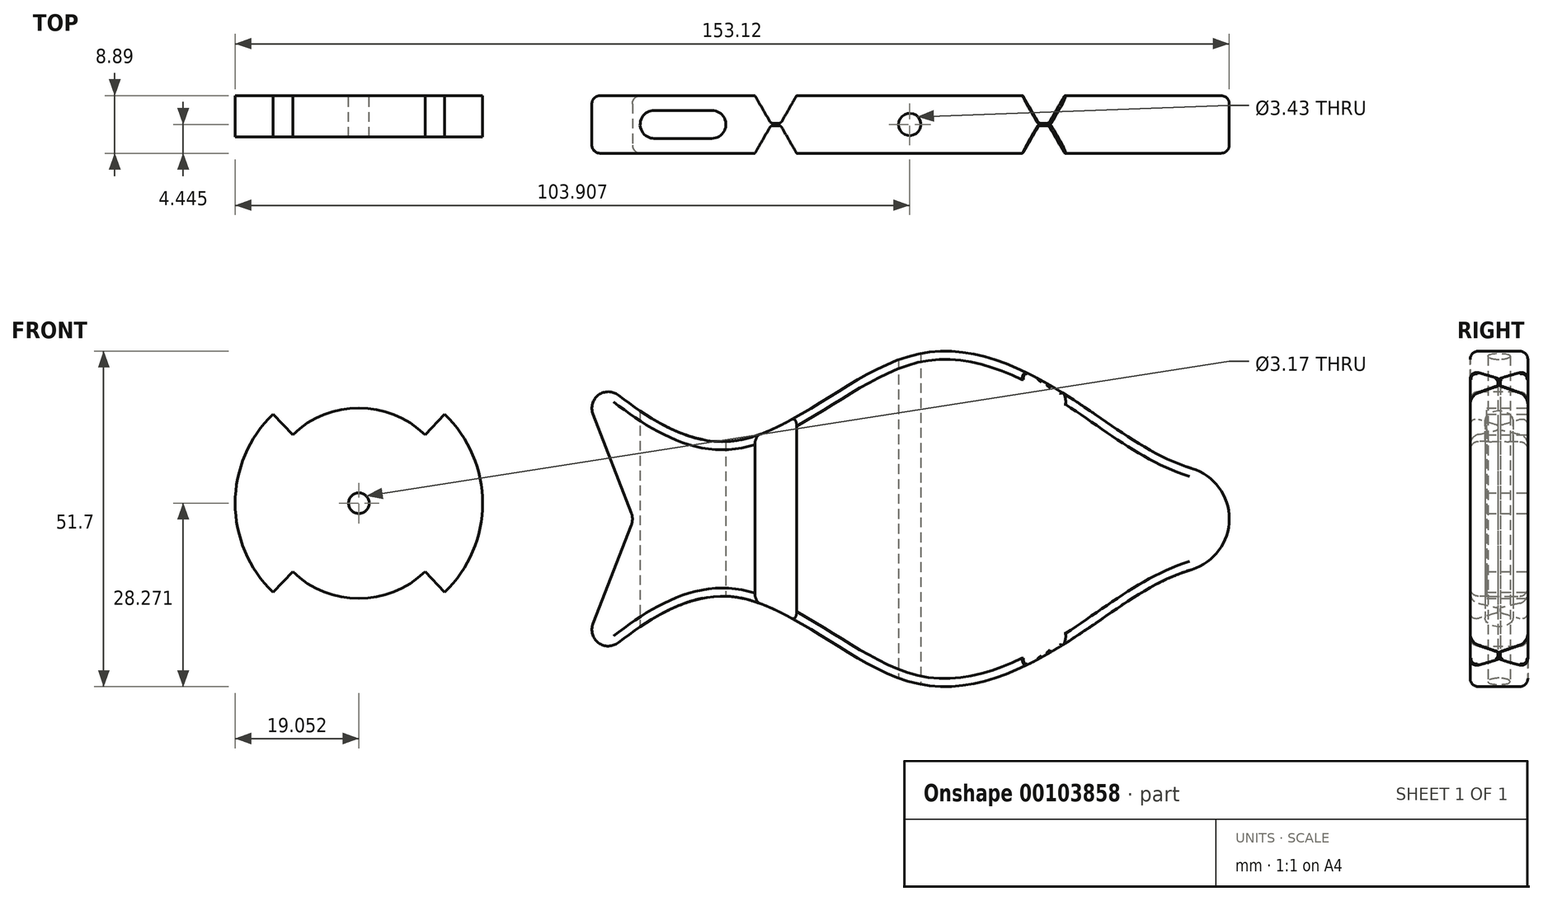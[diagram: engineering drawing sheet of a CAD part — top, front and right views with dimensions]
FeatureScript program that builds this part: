
annotation { "Feature Type Name" : "Feature", "Feature Type Description" : "" }
export const myFeature = defineFeature(function(context is Context, id is Id, definition is map)
    precondition{}
    {
        {
            var Q0;
            Q0=qCreatedBy(makeId("Front.planeOp"),FACE);
            var sketch = newSketch(context, id + "F0", { "sketchPlane" : qUnion([Q0])});
            skLineSegment(sketch, "E0.bottom", {"start": v(0, 0) * mm, "end": v(101.6, 0) * mm, "construction": true});
            skLineSegment(sketch, "E0.top", {"start": v(0, 50.8) * mm, "end": v(101.6, 50.8) * mm, "construction": true});
            skLineSegment(sketch, "E0.left", {"start": v(0, 0) * mm, "end": v(0, 50.8) * mm, "construction": true});
            skLineSegment(sketch, "E0.right", {"start": v(101.6, 0) * mm, "end": v(101.6, 50.8) * mm, "construction": true});
            skArc(sketch, "E1", {"start": v(101.6, 25.4) * mm, "mid": v(100, 30.23) * mm, "end": v(95.86, 33.18) * mm});
            skPoint(sketch, "E1.centerSnap0", {"position": v(101.6, 25.4) * mm});
            skFitSpline(sketch, "E2", {"points": [v(95.86, 33.18) * mm, v(77.9, 43.57) * mm, v(53.58, 50.8) * mm, v(25.25, 37.41) * mm, v(0, 50.8) * mm], "startDerivative": vector(-90.13, 27.78) * mm, "endDerivative": vector(-94.96, 83.29) * mm});
            skLineSegment(sketch, "E3", {"start": v(101.6, 25.4) * mm, "end": v(0, 25.4) * mm, "construction": true});
            skFitSpline(sketch, "E4.MirrorCS", {"points": [v(95.86, 17.62) * mm, v(77.9, 7.23) * mm, v(53.58, 0) * mm, v(25.25, 13.39) * mm, v(0, 0) * mm], "startDerivative": vector(-90.13, -27.78) * mm, "endDerivative": vector(-94.96, -83.29) * mm});
            skArc(sketch, "E5.MirrorCS", {"start": v(101.6, 25.4) * mm, "mid": v(100, 20.57) * mm, "end": v(95.86, 17.62) * mm});
            skLineSegment(sketch, "E6", {"start": v(0, 50.8) * mm, "end": v(9.85, 25.4) * mm});
            skLineSegment(sketch, "E7", {"start": v(9.85, 25.4) * mm, "end": v(0, 0) * mm});
            skSolve(sketch);
        }
        {
            var Q0;
            Q0=makeQuery(id+"F0.imprint","IMPRINT",FACE,{"disambiguationData":[TD([[makeQuery(id+"F0.imprint","IMPRINT",EDGE,{"derivedFrom":sQuery(id+"F0.wireOp",EDGE,"E1")}),1.0]])]});
            extrude(context, id + "F1", {"entities" : qUnion([Q0]), "depth" : 8.9 * mm});
        }
        {
            var Q0;
            Q0=qCreatedBy(makeId("Top.planeOp"),FACE);
            var sketch = newSketch(context, id + "F2", { "sketchPlane" : qUnion([Q0])});
            skFitSpline(sketch, "E8.0", {"points": [v(95.86, -8.9) * mm, v(89.2, -8.9) * mm, v(78.75, -8.9) * mm, v(52.6, -8.9) * mm, v(25.22, -8.9) * mm, v(8.24, -8.9) * mm, v(0, -8.9) * mm], "construction": true});
            skFitSpline(sketch, "E9.0", {"points": [v(95.86, 0) * mm, v(89.2, 0) * mm, v(78.75, 0) * mm, v(52.6, 0) * mm, v(25.22, 0) * mm, v(8.24, 0) * mm, v(0, 0) * mm], "construction": true});
            skLineSegment(sketch, "E10", {"start": v(0, 0) * mm, "end": v(0, -8.9) * mm, "construction": true});
            skLineSegment(sketch, "E11", {"start": v(0, -4.45) * mm, "end": v(95.86, -4.45) * mm, "construction": true});
            skLineSegment(sketch, "E12", {"start": v(28.53, 0) * mm, "end": v(30.99, -4.25) * mm});
            skLineSegment(sketch, "E13", {"start": v(30.99, -4.25) * mm, "end": v(32.51, -4.25) * mm});
            skLineSegment(sketch, "E14", {"start": v(32.51, -4.25) * mm, "end": v(34.97, 0) * mm});
            skLineSegment(sketch, "E15", {"start": v(31.75, -4.25) * mm, "end": v(31.75, 0) * mm, "construction": true});
            skLineSegment(sketch, "E16", {"start": v(28.53, 0) * mm, "end": v(34.97, 0) * mm});
            skLineSegment(sketch, "E17.MirrorCS", {"start": v(30.99, -4.64) * mm, "end": v(32.51, -4.64) * mm});
            skLineSegment(sketch, "E18.MirrorCS", {"start": v(32.51, -4.64) * mm, "end": v(34.97, -8.9) * mm});
            skLineSegment(sketch, "E19.MirrorCS", {"start": v(28.53, -8.9) * mm, "end": v(34.97, -8.9) * mm});
            skLineSegment(sketch, "E20.MirrorCS", {"start": v(28.53, -8.9) * mm, "end": v(30.99, -4.64) * mm});
            skLineSegment(sketch, "E21.MirrorCS", {"start": v(31.75, -4.64) * mm, "end": v(31.75, -8.9) * mm, "construction": true});
            skLineSegment(sketch, "E22.1.0.0", {"start": v(73.03, -4.64) * mm, "end": v(73.03, -8.9) * mm, "construction": true});
            skLineSegment(sketch, "E22.1.0.1", {"start": v(69.8, 0) * mm, "end": v(76.24, 0) * mm});
            skLineSegment(sketch, "E22.1.0.2", {"start": v(73.79, -4.64) * mm, "end": v(76.24, -8.9) * mm});
            skLineSegment(sketch, "E22.1.0.3", {"start": v(69.8, -8.9) * mm, "end": v(76.24, -8.9) * mm});
            skLineSegment(sketch, "E22.1.0.4", {"start": v(73.79, -4.25) * mm, "end": v(76.24, 0) * mm});
            skLineSegment(sketch, "E22.1.0.5", {"start": v(69.8, 0) * mm, "end": v(72.26, -4.25) * mm});
            skLineSegment(sketch, "E22.1.0.6", {"start": v(73.03, -4.25) * mm, "end": v(73.03, 0) * mm, "construction": true});
            skLineSegment(sketch, "E22.1.0.7", {"start": v(69.8, -8.89) * mm, "end": v(72.26, -4.64) * mm});
            skLineSegment(sketch, "E22.1.0.8", {"start": v(72.26, -4.64) * mm, "end": v(73.79, -4.64) * mm});
            skLineSegment(sketch, "E22.1.0.9", {"start": v(72.26, -4.25) * mm, "end": v(73.79, -4.25) * mm});
            skLineSegment(sketch, "E22.direction1", {"start": v(28.53, -8.9) * mm, "end": v(69.8, -8.9) * mm, "construction": true});
            skLineSegment(sketch, "E23", {"start": v(31.75, 0) * mm, "end": v(73.03, 0) * mm, "construction": true});
            skLineSegment(sketch, "E24", {"start": v(52.39, 0) * mm, "end": v(52.39, -8.9) * mm, "construction": true});
            skCircle(sketch, "E25", {"center": v(52.39, -4.45) * mm, "radius": 1.71 * mm});
            skArc(sketch, "E26", {"start": v(21.9, -6.6) * mm, "mid": v(24.07, -4.45) * mm, "end": v(21.9, -2.29) * mm});
            skArc(sketch, "E27", {"start": v(13.02, -2.29) * mm, "mid": v(10.86, -4.45) * mm, "end": v(13.02, -6.6) * mm});
            skLineSegment(sketch, "E28", {"start": v(13.02, -6.6) * mm, "end": v(13.02, -2.29) * mm, "construction": true});
            skLineSegment(sketch, "E29", {"start": v(13.02, -2.29) * mm, "end": v(21.9, -2.29) * mm});
            skLineSegment(sketch, "E30", {"start": v(21.9, -2.29) * mm, "end": v(21.9, -6.6) * mm, "construction": true});
            skLineSegment(sketch, "E31", {"start": v(21.9, -6.6) * mm, "end": v(13.02, -6.6) * mm});
            skArc(sketch, "E32.MirrorCS", {"start": v(82.87, -6.6) * mm, "mid": v(80.7, -4.45) * mm, "end": v(82.87, -2.29) * mm});
            skLineSegment(sketch, "E33.MirrorCS", {"start": v(91.76, -6.6) * mm, "end": v(91.76, -2.29) * mm, "construction": true});
            skLineSegment(sketch, "E34.MirrorCS", {"start": v(82.87, -2.29) * mm, "end": v(82.87, -6.6) * mm, "construction": true});
            skLineSegment(sketch, "E35.MirrorCS", {"start": v(82.87, -6.6) * mm, "end": v(91.76, -6.6) * mm});
            skArc(sketch, "E36.MirrorCS", {"start": v(91.76, -2.29) * mm, "mid": v(93.92, -4.45) * mm, "end": v(91.76, -6.6) * mm});
            skLineSegment(sketch, "E37.MirrorCS", {"start": v(91.76, -2.29) * mm, "end": v(82.87, -2.29) * mm});
            skSolve(sketch);
        }
        {
            var Q0;
            Q0=makeQuery(id+"F2.imprint","IMPRINT",FACE,{"disambiguationData":[TD([[makeQuery(id+"F2.imprint","IMPRINT",EDGE,{"derivedFrom":sQuery(id+"F2.wireOp",EDGE,"x2erziiV-STz7-uTo3-0Nw2-tx1kgwy7OqIq")}),1.0]])]});
            var Q1;
            Q1=makeQuery(id+"F2.imprint","IMPRINT",FACE,{"disambiguationData":[TD([[makeQuery(id+"F2.imprint","IMPRINT",EDGE,{"derivedFrom":sQuery(id+"F2.wireOp",EDGE,"2GcT3ghf-DHIi-GQC9-RQm8-pTAT7ZEsl3gv")}),1.0]])]});
            var Q2;
            Q2=makeQuery(id+"F2.imprint","IMPRINT",FACE,{"disambiguationData":[TD([[makeQuery(id+"F2.imprint","IMPRINT",EDGE,{"derivedFrom":sQuery(id+"F2.wireOp",EDGE,"E25")}),1.0]])]});
            var Q3;
            Q3=makeQuery(id+"F2.imprint","IMPRINT",FACE,{"disambiguationData":[TD([[makeQuery(id+"F2.imprint","IMPRINT",EDGE,{"derivedFrom":sQuery(id+"F2.wireOp",EDGE,"E12")}),1.0]])]});
            var Q4;
            Q4=makeQuery(id+"F2.imprint","IMPRINT",FACE,{"disambiguationData":[TD([[makeQuery(id+"F2.imprint","IMPRINT",EDGE,{"derivedFrom":sQuery(id+"F2.wireOp",EDGE,"E17.MirrorCS")}),-1.0]])]});
            var Q5;
            Q5=makeQuery(id+"F2.imprint","IMPRINT",FACE,{"disambiguationData":[TD([[makeQuery(id+"F2.imprint","IMPRINT",EDGE,{"derivedFrom":sQuery(id+"F2.wireOp",EDGE,"E22.1.0.2")}),-1.0]])]});
            var Q6;
            Q6=makeQuery(id+"F2.imprint","IMPRINT",FACE,{"disambiguationData":[TD([[makeQuery(id+"F2.imprint","IMPRINT",EDGE,{"derivedFrom":sQuery(id+"F2.wireOp",EDGE,"E22.1.0.1")}),-1.0]])]});
            var Q7;
            Q7=makeQuery(id+"F2.imprint","IMPRINT",FACE,{"disambiguationData":[TD([[makeQuery(id+"F2.imprint","IMPRINT",EDGE,{"derivedFrom":sQuery(id+"F2.wireOp",EDGE,"E26")}),1.0]])]});
            var Q8;
            Q8=makeQuery(id+"F2.imprint","IMPRINT",FACE,{"disambiguationData":[TD([[makeQuery(id+"F2.imprint","IMPRINT",EDGE,{"derivedFrom":sQuery(id+"F2.wireOp",EDGE,"E32.MirrorCS")}),-1.0]])]});
            extrude(context, id + "F3", {"entities" : qUnion([Q0, Q1, Q2, Q3, Q4, Q5, Q6, Q7, Q8]), "operationType" : NewBodyOperationType.REMOVE, "endBound" : BoundingType.THROUGH_ALL, "depth" : 25.4 * mm, "hasSecondDirection" : true, "secondDirectionBound" : SecondDirectionBoundingType.THROUGH_ALL, "secondDirectionOppositeDirection" : true, "secondDirectionDepth" : 25.4 * mm});
        }
        {
            var Q0;
            Q0=makeQuery(id+"F1.opExtrude","SWEPT_EDGE",EDGE,{"disambiguationData":[OSD([sQuery(id+"F0.wireOp",EDGE,"E2"),sQuery(id+"F0.wireOp",EDGE,"E6")])]});
            var Q1;
            Q1=makeQuery(id+"F1.opExtrude","SWEPT_EDGE",EDGE,{"disambiguationData":[OSD([sQuery(id+"F0.wireOp",EDGE,"E4.MirrorCS"),sQuery(id+"F0.wireOp",EDGE,"E7")])]});
            var Q2;
            Q2=makeQuery(id+"F1.opExtrude","SWEPT_EDGE",EDGE,{"disambiguationData":[OSD([sQuery(id+"F0.wireOp",EDGE,"E6"),sQuery(id+"F0.wireOp",EDGE,"E7")])]});
            fillet(context, id + "F4", {"entities" : qUnion([Q0, Q1, Q2]), "radius" : 2.54 * mm, "tangentPropagation" : true, "allowEdgeOverflow" : false});
        }
        {
            var Q0;
            Q0=makeQuery(id+"F1.opExtrude","CAP_EDGE",EDGE,{"disambiguationData":[OSD([sQuery(id+"F0.wireOp",EDGE,"E2")])],"isStart":false});
            var Q1;
            Q1=makeQuery(id+"F1.opExtrude","CAP_EDGE",EDGE,{"disambiguationData":[OSD([sQuery(id+"F0.wireOp",EDGE,"E2")])],"isStart":true});
            var Q2;
            {var subQ0=sQuery(id+"F0.wireOp",EDGE,"E4.MirrorCS");Q2=makeQuery(id+"F3.boolean.opBoolean","SPLIT",EDGE,{"disambiguationData":[TD([makeQuery(id+"F3.opExtrude","SWEPT_FACE",FACE,{"disambiguationData":[OSD([sQuery(id+"F2.wireOp",EDGE,"E18.MirrorCS")])]})])],"derivedFrom":makeQuery(id+"F1.opExtrude","CAP_EDGE",EDGE,{"disambiguationData":[OSD([subQ0])],"isStart":false})});}
            var Q3;
            {var subQ0=sQuery(id+"F0.wireOp",EDGE,"E4.MirrorCS");Q3=makeQuery(id+"F3.boolean.opBoolean","SPLIT",EDGE,{"disambiguationData":[TD([makeQuery(id+"F3.opExtrude","SWEPT_FACE",FACE,{"disambiguationData":[OSD([sQuery(id+"F2.wireOp",EDGE,"E14")])]})])],"derivedFrom":makeQuery(id+"F1.opExtrude","CAP_EDGE",EDGE,{"disambiguationData":[OSD([subQ0])],"isStart":true})});}
            fillet(context, id + "F5", {"entities" : qUnion([Q0, Q1, Q2, Q3]), "radius" : 1.27 * mm, "tangentPropagation" : true, "allowEdgeOverflow" : false});
        }
        {
            var Q0;
            Q0=makeQuery(id+"F3.boolean.opBoolean","COPY",EDGE,{"derivedFrom":makeQuery(id+"F3.opExtrude","SWEPT_EDGE",EDGE,{"disambiguationData":[OSD([sQuery(id+"F2.wireOp",EDGE,"E17.MirrorCS"),sQuery(id+"F2.wireOp",EDGE,"E20.MirrorCS")])]})});
            var Q1;
            Q1=makeQuery(id+"F3.boolean.opBoolean","COPY",EDGE,{"derivedFrom":makeQuery(id+"F3.opExtrude","SWEPT_EDGE",EDGE,{"disambiguationData":[OSD([sQuery(id+"F2.wireOp",EDGE,"E17.MirrorCS"),sQuery(id+"F2.wireOp",EDGE,"E18.MirrorCS")])]})});
            var Q2;
            Q2=makeQuery(id+"F3.boolean.opBoolean","COPY",EDGE,{"derivedFrom":makeQuery(id+"F3.opExtrude","SWEPT_EDGE",EDGE,{"disambiguationData":[OSD([sQuery(id+"F2.wireOp",EDGE,"E12"),sQuery(id+"F2.wireOp",EDGE,"E13")])]})});
            var Q3;
            Q3=makeQuery(id+"F3.boolean.opBoolean","COPY",EDGE,{"derivedFrom":makeQuery(id+"F3.opExtrude","SWEPT_EDGE",EDGE,{"disambiguationData":[OSD([sQuery(id+"F2.wireOp",EDGE,"E13"),sQuery(id+"F2.wireOp",EDGE,"E14")])]})});
            var Q4;
            Q4=makeQuery(id+"F3.boolean.opBoolean","COPY",EDGE,{"derivedFrom":makeQuery(id+"F3.opExtrude","SWEPT_EDGE",EDGE,{"disambiguationData":[OSD([sQuery(id+"F2.wireOp",EDGE,"E22.1.0.7"),sQuery(id+"F2.wireOp",EDGE,"E22.1.0.8")])]})});
            var Q5;
            Q5=makeQuery(id+"F3.boolean.opBoolean","COPY",EDGE,{"derivedFrom":makeQuery(id+"F3.opExtrude","SWEPT_EDGE",EDGE,{"disambiguationData":[OSD([sQuery(id+"F2.wireOp",EDGE,"E22.1.0.2"),sQuery(id+"F2.wireOp",EDGE,"E22.1.0.8")])]})});
            var Q6;
            Q6=makeQuery(id+"F3.boolean.opBoolean","COPY",EDGE,{"derivedFrom":makeQuery(id+"F3.opExtrude","SWEPT_EDGE",EDGE,{"disambiguationData":[OSD([sQuery(id+"F2.wireOp",EDGE,"E22.1.0.5"),sQuery(id+"F2.wireOp",EDGE,"E22.1.0.9")])]})});
            var Q7;
            Q7=makeQuery(id+"F3.boolean.opBoolean","COPY",EDGE,{"derivedFrom":makeQuery(id+"F3.opExtrude","SWEPT_EDGE",EDGE,{"disambiguationData":[OSD([sQuery(id+"F2.wireOp",EDGE,"E22.1.0.4"),sQuery(id+"F2.wireOp",EDGE,"E22.1.0.9")])]})});
            fillet(context, id + "F6", {"entities" : qUnion([Q0, Q1, Q2, Q3, Q4, Q5, Q6, Q7]), "radius" : 0.5 * mm, "tangentPropagation" : true, "allowEdgeOverflow" : false});
        }
        {
            var Q0;
            Q0=makeQuery(id+"F3.boolean.opBoolean","COPY",EDGE,{"derivedFrom":makeQuery(id+"F3.opExtrude","SWEPT_EDGE",EDGE,{"disambiguationData":[OSD([sQuery(id+"F2.wireOp",EDGE,"E19.MirrorCS"),sQuery(id+"F2.wireOp",EDGE,"E20.MirrorCS")])]})});
            var Q1;
            Q1=makeQuery(id+"F3.boolean.opBoolean","COPY",EDGE,{"derivedFrom":makeQuery(id+"F3.opExtrude","SWEPT_EDGE",EDGE,{"disambiguationData":[OSD([sQuery(id+"F2.wireOp",EDGE,"E22.1.0.3"),sQuery(id+"F2.wireOp",EDGE,"E22.1.0.7")])]})});
            var Q2;
            Q2=makeQuery(id+"F3.boolean.opBoolean","COPY",EDGE,{"derivedFrom":makeQuery(id+"F3.opExtrude","SWEPT_EDGE",EDGE,{"disambiguationData":[OSD([sQuery(id+"F2.wireOp",EDGE,"E12"),sQuery(id+"F2.wireOp",EDGE,"E16")])]})});
            var Q3;
            Q3=makeQuery(id+"F3.boolean.opBoolean","COPY",EDGE,{"derivedFrom":makeQuery(id+"F3.opExtrude","SWEPT_EDGE",EDGE,{"disambiguationData":[OSD([sQuery(id+"F2.wireOp",EDGE,"E22.1.0.1"),sQuery(id+"F2.wireOp",EDGE,"E22.1.0.5")])]})});
            fillet(context, id + "F7", {"entities" : qUnion([Q0, Q1, Q2, Q3]), "radius" : 0.25 * mm, "tangentPropagation" : true, "allowEdgeOverflow" : false});
        }
        {
            var Q0;
            Q0=qCreatedBy(makeId("Front.planeOp"),FACE);
            var sketch = newSketch(context, id + "F8", { "sketchPlane" : qUnion([Q0])});
            skCircle(sketch, "E38", {"center": v(-32.47, 27.82) * mm, "radius": 19.05 * mm});
            skLineSegment(sketch, "E39", {"start": v(-32.47, 27.82) * mm, "end": v(-19.24, 41.52) * mm, "construction": true});
            skLineSegment(sketch, "E40", {"start": v(-51.52, 27.82) * mm, "end": v(-13.42, 27.82) * mm, "construction": true});
            skLineSegment(sketch, "E41", {"start": v(-32.47, 8.77) * mm, "end": v(-32.47, 46.87) * mm, "construction": true});
            skLineSegment(sketch, "E42.MirrorCS", {"start": v(-32.47, 27.82) * mm, "end": v(-45.7, 41.52) * mm, "construction": true});
            skLineSegment(sketch, "E43", {"start": v(-45.7, 41.52) * mm, "end": v(-42.66, 38.38) * mm});
            skArc(sketch, "E44", {"start": v(-42.66, 38.38) * mm, "mid": v(-32.47, 42.5) * mm, "end": v(-22.27, 38.38) * mm});
            skLineSegment(sketch, "E45", {"start": v(-22.27, 38.38) * mm, "end": v(-19.24, 41.52) * mm});
            skArc(sketch, "E46.MirrorCS", {"start": v(-42.66, 17.26) * mm, "mid": v(-32.47, 13.15) * mm, "end": v(-22.27, 17.26) * mm});
            skLineSegment(sketch, "E47.MirrorCS", {"start": v(-22.27, 17.26) * mm, "end": v(-19.24, 14.12) * mm});
            skLineSegment(sketch, "E48.MirrorCS", {"start": v(-45.7, 14.12) * mm, "end": v(-42.66, 17.26) * mm});
            skCircle(sketch, "E49", {"center": v(-32.47, 27.82) * mm, "radius": 1.59 * mm});
            skSolve(sketch);
        }
        {
            var Q0;
            {var subQ0=sQuery(id+"F8.wireOp",EDGE,"E43");Q0=makeQuery(id+"F8.imprint","IMPRINT",FACE,{"disambiguationData":[TD([[makeQuery(id+"F8.imprint","IMPRINT",EDGE,{"derivedFrom":subQ0}),-1.0]])]});}
            extrude(context, id + "F9", {"entities" : qUnion([Q0]), "depth" : 6.35 * mm});
        }
    });
